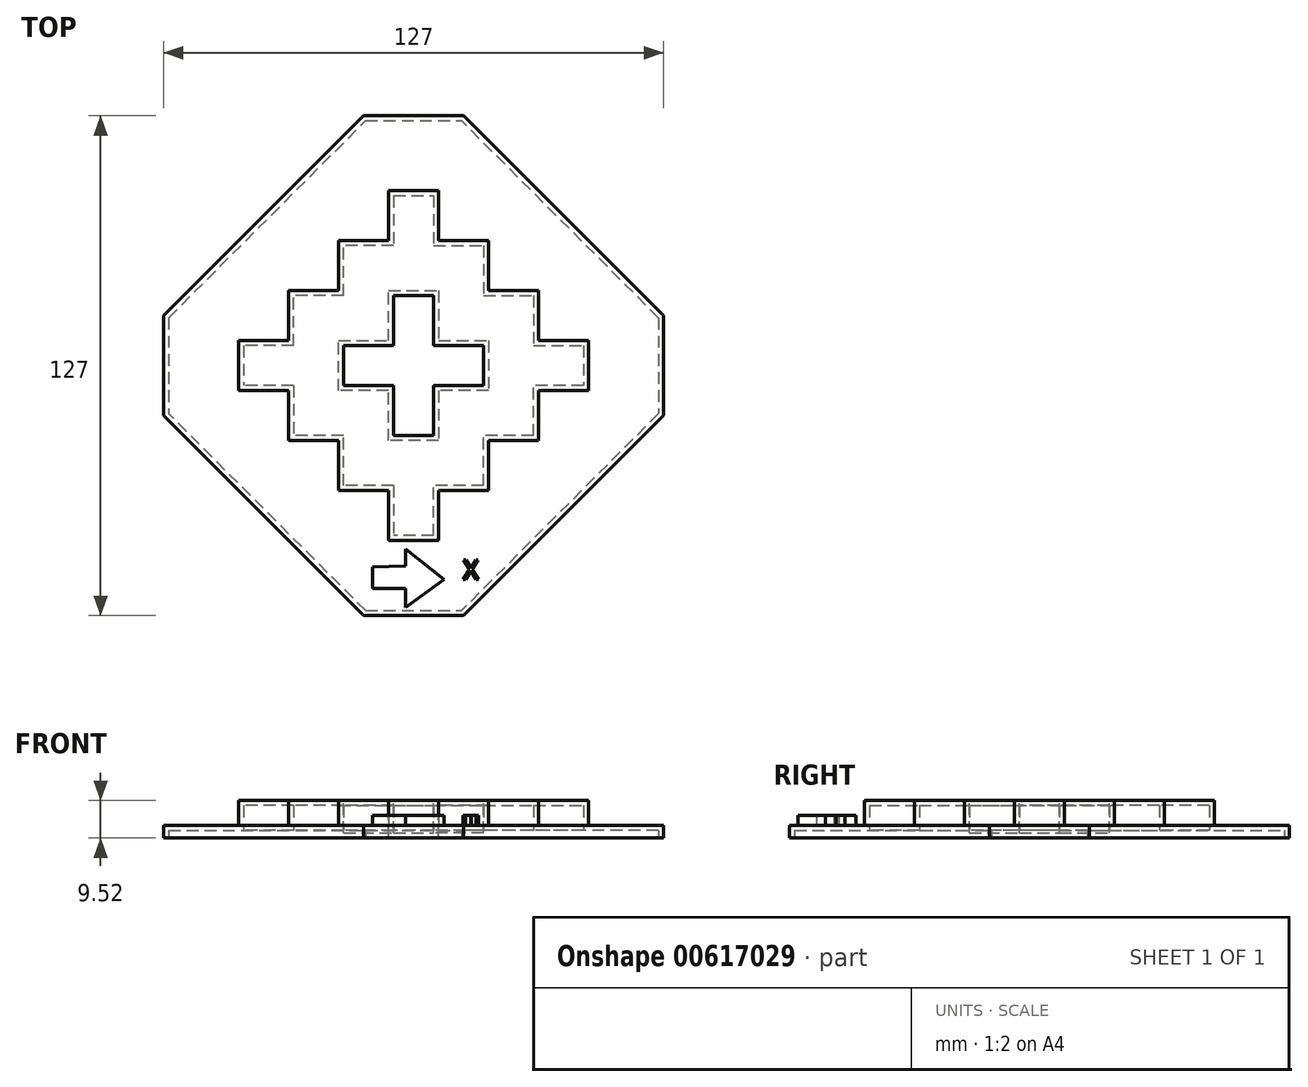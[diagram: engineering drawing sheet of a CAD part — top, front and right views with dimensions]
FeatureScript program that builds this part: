
annotation { "Feature Type Name" : "Feature", "Feature Type Description" : "" }
export const myFeature = defineFeature(function(context is Context, id is Id, definition is map)
    precondition{}
    {
        {
            var Q0;
            Q0=qCreatedBy(makeId("Top.planeOp"),FACE);
            var sketch = newSketch(context, id + "F0", { "sketchPlane" : qUnion([Q0])});
            skLineSegment(sketch, "E0", {"start": v(-25.4, 127) * mm, "end": v(25.4, 127) * mm});
            skLineSegment(sketch, "E1", {"start": v(127, 25.4) * mm, "end": v(127, -25.4) * mm});
            skLineSegment(sketch, "E2", {"start": v(-25.4, -127) * mm, "end": v(25.4, -127) * mm});
            skLineSegment(sketch, "E3", {"start": v(-127, 25.4) * mm, "end": v(-127, -25.4) * mm});
            skLineSegment(sketch, "E4", {"start": v(-127, 25.4) * mm, "end": v(-25.4, 127) * mm});
            skLineSegment(sketch, "E5", {"start": v(127, 25.4) * mm, "end": v(25.4, 127) * mm});
            skLineSegment(sketch, "E6", {"start": v(127, -25.4) * mm, "end": v(25.4, -127) * mm});
            skLineSegment(sketch, "E7", {"start": v(-25.4, -127) * mm, "end": v(-127, -25.4) * mm});
            skSolve(sketch);
        }
        {
            var Q0;
            Q0 = qSketchRegion(id + "F0", true);
            extrude(context, id + "F1", {"entities" : qUnion([Q0]), "depth" : 6.35 * mm, "offsetDistance" : 25.4 * mm});
        }
        {
            var Q0;
            Q0=makeQuery(id+"F1.opExtrude","CAP_FACE",FACE,{"disambiguationData":[OSD([sQuery(id+"F0.wireOp",EDGE,"E0"),sQuery(id+"F0.wireOp",EDGE,"E1"),sQuery(id+"F0.wireOp",EDGE,"E2"),sQuery(id+"F0.wireOp",EDGE,"E3"),sQuery(id+"F0.wireOp",EDGE,"E4"),sQuery(id+"F0.wireOp",EDGE,"E5"),sQuery(id+"F0.wireOp",EDGE,"E6"),sQuery(id+"F0.wireOp",EDGE,"E7")])],"isStart":true});
            shell(context, id + "F2", {"entities" : qUnion([Q0]), "thickness" : 2.54 * mm});
        }
        {
            var Q0;
            Q0=makeQuery(id+"F1.opExtrude","CAP_FACE",FACE,{"disambiguationData":[OSD([sQuery(id+"F0.wireOp",EDGE,"E0"),sQuery(id+"F0.wireOp",EDGE,"E1"),sQuery(id+"F0.wireOp",EDGE,"E2"),sQuery(id+"F0.wireOp",EDGE,"E3"),sQuery(id+"F0.wireOp",EDGE,"E4"),sQuery(id+"F0.wireOp",EDGE,"E5"),sQuery(id+"F0.wireOp",EDGE,"E6"),sQuery(id+"F0.wireOp",EDGE,"E7")])],"isStart":false});
            var sketch = newSketch(context, id + "F3", { "sketchPlane" : qUnion([Q0])});
            skLineSegment(sketch, "E8", {"start": v(-12.7, 88.9) * mm, "end": v(12.7, 88.9) * mm});
            skLineSegment(sketch, "E9", {"start": v(-12.7, 88.9) * mm, "end": v(-12.7, 63.5) * mm});
            skLineSegment(sketch, "E10", {"start": v(12.7, 88.9) * mm, "end": v(12.7, 63.5) * mm});
            skLineSegment(sketch, "E11", {"start": v(12.7, 63.5) * mm, "end": v(38.1, 63.5) * mm});
            skLineSegment(sketch, "E12", {"start": v(38.1, 63.5) * mm, "end": v(38.1, 38.1) * mm});
            skLineSegment(sketch, "E13", {"start": v(38.1, 38.1) * mm, "end": v(63.5, 38.1) * mm});
            skLineSegment(sketch, "E14", {"start": v(63.5, 38.1) * mm, "end": v(63.5, 12.7) * mm});
            skLineSegment(sketch, "E15", {"start": v(63.5, 12.7) * mm, "end": v(88.9, 12.7) * mm});
            skLineSegment(sketch, "E16", {"start": v(88.9, 12.7) * mm, "end": v(88.9, -12.7) * mm});
            skLineSegment(sketch, "E17", {"start": v(88.9, -12.7) * mm, "end": v(63.5, -12.7) * mm});
            skLineSegment(sketch, "E18", {"start": v(63.5, -38.1) * mm, "end": v(63.5, -12.7) * mm});
            skLineSegment(sketch, "E19", {"start": v(63.5, -38.1) * mm, "end": v(38.1, -38.1) * mm});
            skLineSegment(sketch, "E20", {"start": v(38.1, -63.5) * mm, "end": v(38.1, -38.1) * mm});
            skLineSegment(sketch, "E21", {"start": v(38.1, -63.5) * mm, "end": v(12.7, -63.5) * mm});
            skLineSegment(sketch, "E22", {"start": v(12.7, -88.9) * mm, "end": v(12.7, -63.5) * mm});
            skLineSegment(sketch, "E23", {"start": v(12.7, -88.9) * mm, "end": v(-12.7, -88.9) * mm});
            skLineSegment(sketch, "E24", {"start": v(-12.7, -63.5) * mm, "end": v(-12.7, -88.9) * mm});
            skLineSegment(sketch, "E25", {"start": v(-12.7, -63.5) * mm, "end": v(-38.1, -63.5) * mm});
            skLineSegment(sketch, "E26", {"start": v(-38.1, -63.5) * mm, "end": v(-38.1, -38.1) * mm});
            skLineSegment(sketch, "E27", {"start": v(-38.1, -38.1) * mm, "end": v(-63.5, -38.1) * mm});
            skLineSegment(sketch, "E28", {"start": v(-63.5, -12.7) * mm, "end": v(-63.5, -38.1) * mm});
            skLineSegment(sketch, "E29", {"start": v(-63.5, -12.7) * mm, "end": v(-88.9, -12.7) * mm});
            skLineSegment(sketch, "E30", {"start": v(-88.9, 12.7) * mm, "end": v(-88.9, -12.7) * mm});
            skLineSegment(sketch, "E31", {"start": v(-63.5, 12.7) * mm, "end": v(-88.9, 12.7) * mm});
            skLineSegment(sketch, "E32", {"start": v(-63.5, 12.7) * mm, "end": v(-63.5, 38.1) * mm});
            skLineSegment(sketch, "E33", {"start": v(-38.1, 38.1) * mm, "end": v(-63.5, 38.1) * mm});
            skLineSegment(sketch, "E34", {"start": v(-38.1, 38.1) * mm, "end": v(-38.1, 63.5) * mm});
            skLineSegment(sketch, "E35", {"start": v(-12.7, 63.5) * mm, "end": v(-38.1, 63.5) * mm});
            skSolve(sketch);
        }
        {
            var Q0;
            Q0 = qSketchRegion(id + "F3", true);
            extrude(context, id + "F4", {"entities" : qUnion([Q0]), "operationType" : NewBodyOperationType.ADD, "depth" : 12.7 * mm, "offsetDistance" : 25.4 * mm});
        }
        {
            var Q0;
            Q0=makeQuery(id+"F2.opShell","OFFSET_FACE",FACE,{"disambiguationData":[OSD([sQuery(id+"F0.wireOp",EDGE,"E0"),sQuery(id+"F0.wireOp",EDGE,"E1"),sQuery(id+"F0.wireOp",EDGE,"E2"),sQuery(id+"F0.wireOp",EDGE,"E3"),sQuery(id+"F0.wireOp",EDGE,"E4"),sQuery(id+"F0.wireOp",EDGE,"E5"),sQuery(id+"F0.wireOp",EDGE,"E6"),sQuery(id+"F0.wireOp",EDGE,"E7")])]});
            shell(context, id + "F5", {"entities" : qUnion([Q0]), "thickness" : 2.54 * mm});
        }
        {
            var Q0;
            Q0=makeQuery(id+"F4.opExtrude","CAP_FACE",FACE,{"disambiguationData":[OSD([sQuery(id+"F3.wireOp",EDGE,"E8"),sQuery(id+"F3.wireOp",EDGE,"E9"),sQuery(id+"F3.wireOp",EDGE,"E10"),sQuery(id+"F3.wireOp",EDGE,"E11"),sQuery(id+"F3.wireOp",EDGE,"E12"),sQuery(id+"F3.wireOp",EDGE,"E13"),sQuery(id+"F3.wireOp",EDGE,"E14"),sQuery(id+"F3.wireOp",EDGE,"E15"),sQuery(id+"F3.wireOp",EDGE,"E16"),sQuery(id+"F3.wireOp",EDGE,"E17"),sQuery(id+"F3.wireOp",EDGE,"E18"),sQuery(id+"F3.wireOp",EDGE,"E19"),sQuery(id+"F3.wireOp",EDGE,"E20"),sQuery(id+"F3.wireOp",EDGE,"E21"),sQuery(id+"F3.wireOp",EDGE,"E22"),sQuery(id+"F3.wireOp",EDGE,"E23"),sQuery(id+"F3.wireOp",EDGE,"E24"),sQuery(id+"F3.wireOp",EDGE,"E25"),sQuery(id+"F3.wireOp",EDGE,"E26"),sQuery(id+"F3.wireOp",EDGE,"E27"),sQuery(id+"F3.wireOp",EDGE,"E28"),sQuery(id+"F3.wireOp",EDGE,"E29"),sQuery(id+"F3.wireOp",EDGE,"E30"),sQuery(id+"F3.wireOp",EDGE,"E31"),sQuery(id+"F3.wireOp",EDGE,"E32"),sQuery(id+"F3.wireOp",EDGE,"E33"),sQuery(id+"F3.wireOp",EDGE,"E34"),sQuery(id+"F3.wireOp",EDGE,"E35")])],"isStart":false});
            var sketch = newSketch(context, id + "F6", { "sketchPlane" : qUnion([Q0])});
            skLineSegment(sketch, "E36", {"start": v(-12.7, 38.1) * mm, "end": v(12.7, 38.1) * mm});
            skLineSegment(sketch, "E37", {"start": v(12.7, 38.1) * mm, "end": v(12.7, 12.7) * mm});
            skLineSegment(sketch, "E38", {"start": v(12.7, 12.7) * mm, "end": v(38.1, 12.7) * mm});
            skLineSegment(sketch, "E39", {"start": v(38.1, 12.7) * mm, "end": v(38.1, -12.7) * mm});
            skLineSegment(sketch, "E40", {"start": v(38.1, -12.7) * mm, "end": v(12.7, -12.7) * mm});
            skLineSegment(sketch, "E41", {"start": v(12.7, -12.7) * mm, "end": v(12.7, -38.1) * mm});
            skLineSegment(sketch, "E42", {"start": v(12.7, -38.1) * mm, "end": v(-12.7, -38.1) * mm});
            skLineSegment(sketch, "E43", {"start": v(-12.7, -38.1) * mm, "end": v(-12.7, -12.7) * mm});
            skLineSegment(sketch, "E44", {"start": v(-12.7, -12.7) * mm, "end": v(-38.1, -12.7) * mm});
            skLineSegment(sketch, "E45", {"start": v(-38.1, -12.7) * mm, "end": v(-38.1, 12.7) * mm});
            skLineSegment(sketch, "E46", {"start": v(-38.1, 12.7) * mm, "end": v(-12.7, 12.7) * mm});
            skLineSegment(sketch, "E47", {"start": v(-12.7, 12.7) * mm, "end": v(-12.7, 38.1) * mm});
            skSolve(sketch);
        }
        {
            var Q0;
            Q0 = qSketchRegion(id + "F6", true);
            extrude(context, id + "F7", {"entities" : qUnion([Q0]), "operationType" : NewBodyOperationType.ADD, "oppositeDirection" : true, "depth" : 19.05 * mm, "offsetDistance" : 25.4 * mm});
        }
        {
            var Q0;
            Q0=makeQuery(id+"F4.opExtrude","CAP_FACE",FACE,{"disambiguationData":[OSD([sQuery(id+"F3.wireOp",EDGE,"E8"),sQuery(id+"F3.wireOp",EDGE,"E9"),sQuery(id+"F3.wireOp",EDGE,"E10"),sQuery(id+"F3.wireOp",EDGE,"E11"),sQuery(id+"F3.wireOp",EDGE,"E12"),sQuery(id+"F3.wireOp",EDGE,"E13"),sQuery(id+"F3.wireOp",EDGE,"E14"),sQuery(id+"F3.wireOp",EDGE,"E15"),sQuery(id+"F3.wireOp",EDGE,"E16"),sQuery(id+"F3.wireOp",EDGE,"E17"),sQuery(id+"F3.wireOp",EDGE,"E18"),sQuery(id+"F3.wireOp",EDGE,"E19"),sQuery(id+"F3.wireOp",EDGE,"E20"),sQuery(id+"F3.wireOp",EDGE,"E21"),sQuery(id+"F3.wireOp",EDGE,"E22"),sQuery(id+"F3.wireOp",EDGE,"E23"),sQuery(id+"F3.wireOp",EDGE,"E24"),sQuery(id+"F3.wireOp",EDGE,"E25"),sQuery(id+"F3.wireOp",EDGE,"E26"),sQuery(id+"F3.wireOp",EDGE,"E27"),sQuery(id+"F3.wireOp",EDGE,"E28"),sQuery(id+"F3.wireOp",EDGE,"E29"),sQuery(id+"F3.wireOp",EDGE,"E30"),sQuery(id+"F3.wireOp",EDGE,"E31"),sQuery(id+"F3.wireOp",EDGE,"E32"),sQuery(id+"F3.wireOp",EDGE,"E33"),sQuery(id+"F3.wireOp",EDGE,"E34"),sQuery(id+"F3.wireOp",EDGE,"E35")])],"isStart":false});
            shell(context, id + "F8", {"entities" : qUnion([Q0]), "thickness" : 2.54 * mm});
        }
        {
            var Q0;
            Q0=makeQuery(id+"F1.opExtrude","CAP_FACE",FACE,{"disambiguationData":[OSD([sQuery(id+"F0.wireOp",EDGE,"E0"),sQuery(id+"F0.wireOp",EDGE,"E1"),sQuery(id+"F0.wireOp",EDGE,"E2"),sQuery(id+"F0.wireOp",EDGE,"E3"),sQuery(id+"F0.wireOp",EDGE,"E4"),sQuery(id+"F0.wireOp",EDGE,"E5"),sQuery(id+"F0.wireOp",EDGE,"E6"),sQuery(id+"F0.wireOp",EDGE,"E7")])],"isStart":false});
            var sketch = newSketch(context, id + "F9", { "sketchPlane" : qUnion([Q0])});
            skLineSegment(sketch, "E48", {"start": v(-20.82, -102.29) * mm, "end": v(-20.82, -113.21) * mm});
            skLineSegment(sketch, "E49", {"start": v(-20.82, -113.21) * mm, "end": v(-3.98, -113.21) * mm});
            skLineSegment(sketch, "E50", {"start": v(-3.98, -113.21) * mm, "end": v(-3.98, -122.77) * mm});
            skLineSegment(sketch, "E51", {"start": v(-3.98, -122.77) * mm, "end": v(15.59, -108.66) * mm});
            skLineSegment(sketch, "E52", {"start": v(15.59, -108.66) * mm, "end": v(-3.98, -93.19) * mm});
            skLineSegment(sketch, "E53", {"start": v(-3.98, -93.19) * mm, "end": v(-3.98, -101.83) * mm});
            skLineSegment(sketch, "E54", {"start": v(-3.98, -101.83) * mm, "end": v(-20.82, -102.29) * mm});
            skText(sketch, "E55", { "text": "X", "fontName": "OpenSans-Regular.ttf"});
            const initialGuessF9  = {"E55": [0.02515, -0.10866, 1, 0, 0.01001]};
            skSetInitialGuess(sketch, initialGuessF9);
            skSolve(sketch);
        }
        {
            var Q0;
            Q0 = qSketchRegion(id + "F9", true);
            extrude(context, id + "F10", {"entities" : qUnion([Q0]), "operationType" : NewBodyOperationType.ADD, "depth" : 5.08 * mm, "offsetDistance" : 25.4 * mm});
        }
        {
            var Q0;
            Q0=makeQuery(id+"F1.opExtrude","SWEPT_BODY",BODY,{"disambiguationData":[OSD([sQuery(id+"F0.wireOp",EDGE,"E0"),sQuery(id+"F0.wireOp",EDGE,"E1"),sQuery(id+"F0.wireOp",EDGE,"E2"),sQuery(id+"F0.wireOp",EDGE,"E3"),sQuery(id+"F0.wireOp",EDGE,"E4"),sQuery(id+"F0.wireOp",EDGE,"E5"),sQuery(id+"F0.wireOp",EDGE,"E6"),sQuery(id+"F0.wireOp",EDGE,"E7")])]});
            var Q1;
            Q1=makeQuery(id+"F8.opShell","OFFSET_VERTEX",VERTEX,{"disambiguationData":[OSD([sQuery(id+"F3.wireOp",EDGE,"E8"),sQuery(id+"F3.wireOp",EDGE,"E9"),sQuery(id+"F3.wireOp",EDGE,"E10"),sQuery(id+"F3.wireOp",EDGE,"E11"),sQuery(id+"F3.wireOp",EDGE,"E12"),sQuery(id+"F3.wireOp",EDGE,"E13"),sQuery(id+"F3.wireOp",EDGE,"E14"),sQuery(id+"F3.wireOp",EDGE,"E15"),sQuery(id+"F3.wireOp",EDGE,"E16"),sQuery(id+"F3.wireOp",EDGE,"E17"),sQuery(id+"F3.wireOp",EDGE,"E18"),sQuery(id+"F3.wireOp",EDGE,"E19"),sQuery(id+"F3.wireOp",EDGE,"E20"),sQuery(id+"F3.wireOp",EDGE,"E21"),sQuery(id+"F3.wireOp",EDGE,"E22"),sQuery(id+"F3.wireOp",EDGE,"E23"),sQuery(id+"F3.wireOp",EDGE,"E24"),sQuery(id+"F3.wireOp",EDGE,"E25"),sQuery(id+"F3.wireOp",EDGE,"E26"),sQuery(id+"F3.wireOp",EDGE,"E27"),sQuery(id+"F3.wireOp",EDGE,"E28"),sQuery(id+"F3.wireOp",EDGE,"E29"),sQuery(id+"F3.wireOp",EDGE,"E30"),sQuery(id+"F3.wireOp",EDGE,"E31"),sQuery(id+"F3.wireOp",EDGE,"E32"),sQuery(id+"F3.wireOp",EDGE,"E33"),sQuery(id+"F3.wireOp",EDGE,"E34"),sQuery(id+"F3.wireOp",EDGE,"E35"),sQuery(id+"F6.wireOp",EDGE,"E43"),sQuery(id+"F6.wireOp",EDGE,"E44")])]});
            transform(context, id + "F11", {"entities" : qUnion([Q0]), "transformType" : TransformType.SCALE_UNIFORMLY, "scale" : .5, "scalePoint" : qUnion([Q1]), "makeCopy" : true});
        }
        {
            var Q0;
            Q0=makeQuery(id+"F11.opPattern","COPY",BODY,{"derivedFrom":makeQuery(id+"F1.opExtrude","SWEPT_BODY",BODY,{"disambiguationData":[OSD([sQuery(id+"F0.wireOp",EDGE,"E0"),sQuery(id+"F0.wireOp",EDGE,"E1"),sQuery(id+"F0.wireOp",EDGE,"E2"),sQuery(id+"F0.wireOp",EDGE,"E3"),sQuery(id+"F0.wireOp",EDGE,"E4"),sQuery(id+"F0.wireOp",EDGE,"E5"),sQuery(id+"F0.wireOp",EDGE,"E6"),sQuery(id+"F0.wireOp",EDGE,"E7")])]}),"instanceName":"1"});
            transform(context, id + "F12", {"entities" : qUnion([Q0]), "transformType" : TransformType.TRANSLATION_3D, "dx" : 0 * mm, "dy" : 0 * mm, "dz" : 0 * mm, "makeCopy" : true});
        }
        {
            var Q0;
            Q0=makeQuery(id+"F11.opPattern","COPY",BODY,{"derivedFrom":makeQuery(id+"F1.opExtrude","SWEPT_BODY",BODY,{"disambiguationData":[OSD([sQuery(id+"F0.wireOp",EDGE,"E0"),sQuery(id+"F0.wireOp",EDGE,"E1"),sQuery(id+"F0.wireOp",EDGE,"E2"),sQuery(id+"F0.wireOp",EDGE,"E3"),sQuery(id+"F0.wireOp",EDGE,"E4"),sQuery(id+"F0.wireOp",EDGE,"E5"),sQuery(id+"F0.wireOp",EDGE,"E6"),sQuery(id+"F0.wireOp",EDGE,"E7")])]}),"instanceName":"1"});
            transform(context, id + "F13", {"entities" : qUnion([Q0]), "transformType" : TransformType.TRANSLATION_3D, "dx" : 0 * mm, "dy" : 0 * mm, "dz" : 0 * mm, "makeCopy" : true});
        }
        {
            var Q0;
            Q0=makeQuery(id+"F1.opExtrude","SWEPT_BODY",BODY,{"disambiguationData":[OSD([sQuery(id+"F0.wireOp",EDGE,"E0"),sQuery(id+"F0.wireOp",EDGE,"E1"),sQuery(id+"F0.wireOp",EDGE,"E2"),sQuery(id+"F0.wireOp",EDGE,"E3"),sQuery(id+"F0.wireOp",EDGE,"E4"),sQuery(id+"F0.wireOp",EDGE,"E5"),sQuery(id+"F0.wireOp",EDGE,"E6"),sQuery(id+"F0.wireOp",EDGE,"E7")])]});
            var Q1;
            Q1=makeQuery(id+"F12.opPattern","COPY",BODY,{"derivedFrom":makeQuery(id+"F11.opPattern","COPY",BODY,{"derivedFrom":makeQuery(id+"F1.opExtrude","SWEPT_BODY",BODY,{"disambiguationData":[OSD([sQuery(id+"F0.wireOp",EDGE,"E0"),sQuery(id+"F0.wireOp",EDGE,"E1"),sQuery(id+"F0.wireOp",EDGE,"E2"),sQuery(id+"F0.wireOp",EDGE,"E3"),sQuery(id+"F0.wireOp",EDGE,"E4"),sQuery(id+"F0.wireOp",EDGE,"E5"),sQuery(id+"F0.wireOp",EDGE,"E6"),sQuery(id+"F0.wireOp",EDGE,"E7")])]}),"instanceName":"1"}),"instanceName":"1"});
            var Q2;
            Q2=makeQuery(id+"F13.opPattern","COPY",BODY,{"derivedFrom":makeQuery(id+"F11.opPattern","COPY",BODY,{"derivedFrom":makeQuery(id+"F1.opExtrude","SWEPT_BODY",BODY,{"disambiguationData":[OSD([sQuery(id+"F0.wireOp",EDGE,"E0"),sQuery(id+"F0.wireOp",EDGE,"E1"),sQuery(id+"F0.wireOp",EDGE,"E2"),sQuery(id+"F0.wireOp",EDGE,"E3"),sQuery(id+"F0.wireOp",EDGE,"E4"),sQuery(id+"F0.wireOp",EDGE,"E5"),sQuery(id+"F0.wireOp",EDGE,"E6"),sQuery(id+"F0.wireOp",EDGE,"E7")])]}),"instanceName":"1"}),"instanceName":"1"});
            deleteBodies(context, id + "F14", {"entities" : qUnion([Q0, Q1, Q2])});
        }
    });
